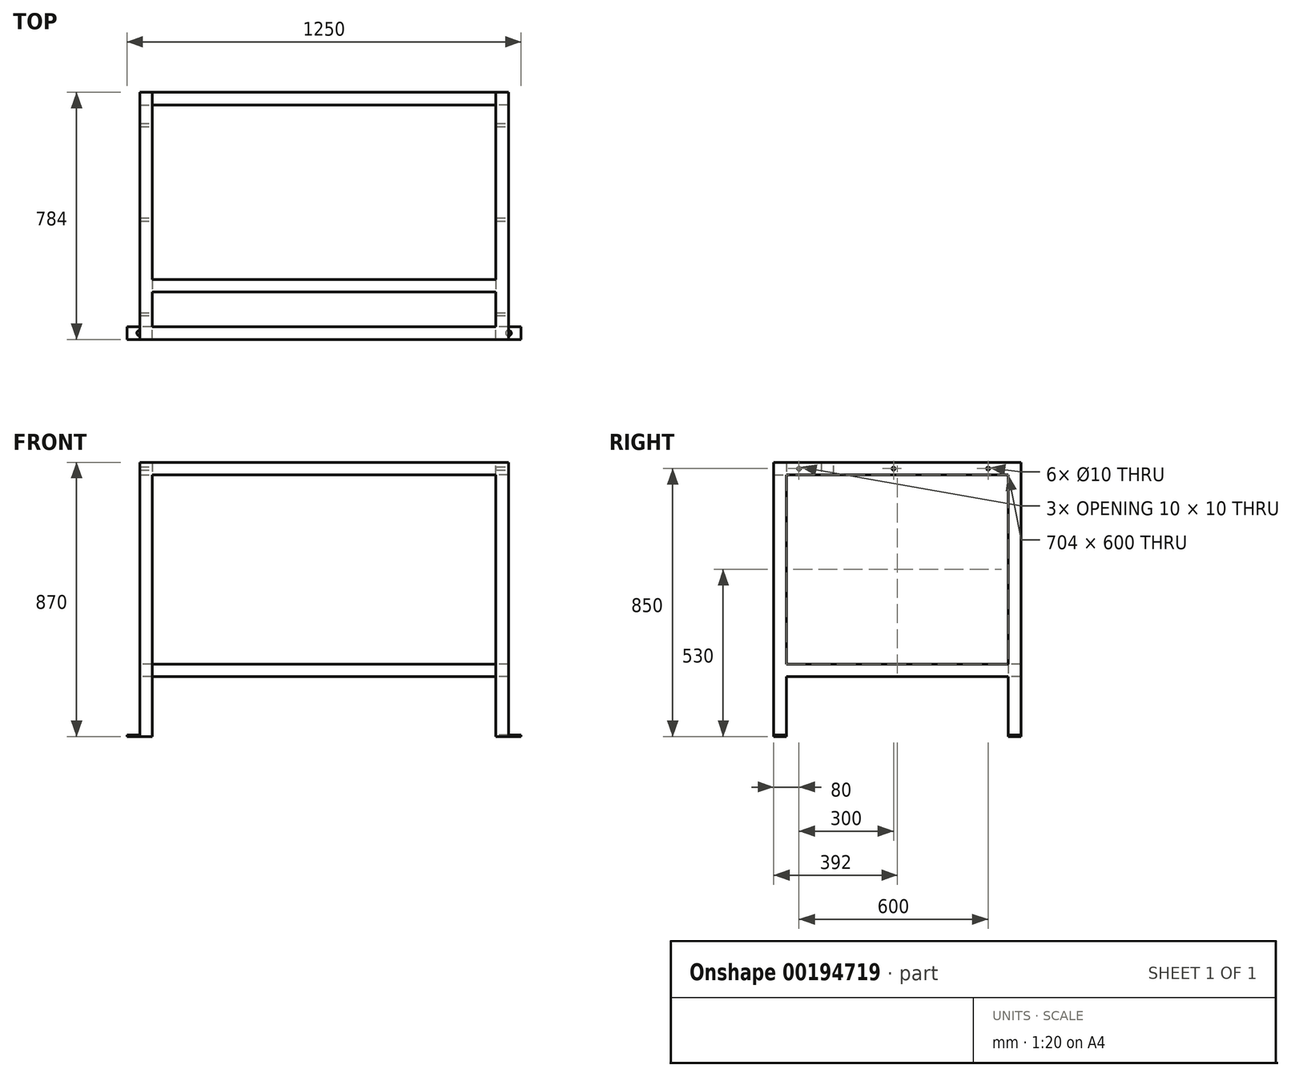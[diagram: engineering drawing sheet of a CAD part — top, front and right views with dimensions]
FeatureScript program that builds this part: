
annotation { "Feature Type Name" : "Feature", "Feature Type Description" : "" }
export const myFeature = defineFeature(function(context is Context, id is Id, definition is map)
    precondition{}
    {
        {
            var Q0;
            Q0=qCreatedBy(makeId("Front.planeOp"),FACE);
            var sketch = newSketch(context, id + "F0", { "sketchPlane" : qUnion([Q0])});
            skLineSegment(sketch, "E0.bottom", {"start": v(-585, -20) * mm, "end": v(585, -20) * mm});
            skLineSegment(sketch, "E0.top", {"start": v(-585, 20) * mm, "end": v(585, 20) * mm});
            skLineSegment(sketch, "E0.left", {"start": v(-585, -20) * mm, "end": v(-585, 20) * mm});
            skLineSegment(sketch, "E0.right", {"start": v(585, -20) * mm, "end": v(585, 20) * mm});
            skPoint(sketch, "E0.middle", {"position": v(0, 0) * mm});
            skLineSegment(sketch, "E1.bottom", {"start": v(-585, -20) * mm, "end": v(-545, -20) * mm});
            skLineSegment(sketch, "E1.top", {"start": v(-585, -850) * mm, "end": v(-545, -850) * mm});
            skLineSegment(sketch, "E1.left", {"start": v(-585, -20) * mm, "end": v(-585, -850) * mm});
            skLineSegment(sketch, "E1.right", {"start": v(-545, -20) * mm, "end": v(-545, -850) * mm});
            skLineSegment(sketch, "E2.bottom", {"start": v(585, -20) * mm, "end": v(545, -20) * mm});
            skLineSegment(sketch, "E2.top", {"start": v(585, -850) * mm, "end": v(545, -850) * mm});
            skLineSegment(sketch, "E2.left", {"start": v(585, -20) * mm, "end": v(585, -850) * mm});
            skLineSegment(sketch, "E2.right", {"start": v(545, -20) * mm, "end": v(545, -850) * mm});
            skLineSegment(sketch, "E3.left", {"start": v(-545, -620) * mm, "end": v(-545, -660) * mm});
            skLineSegment(sketch, "E3.right", {"start": v(545, -620) * mm, "end": v(545, -660) * mm});
            skSolve(sketch);
        }
        {
            var Q0;
            Q0 = qSketchRegion(id + "F0", true);
            extrude(context, id + "F1", {"entities" : qUnion([Q0]), "depth" : 40 * mm});
        }
        {
            var Q0;
            Q0=makeQuery(id+"F1.opExtrude","CAP_FACE",FACE,{"disambiguationData":[OSD([sQuery(id+"F0.wireOp",EDGE,"E0.bottom"),sQuery(id+"F0.wireOp",EDGE,"E0.top"),sQuery(id+"F0.wireOp",EDGE,"E0.left"),sQuery(id+"F0.wireOp",EDGE,"E0.right"),sQuery(id+"F0.wireOp",EDGE,"E1.top"),sQuery(id+"F0.wireOp",EDGE,"E1.left"),sQuery(id+"F0.wireOp",EDGE,"E1.right"),sQuery(id+"F0.wireOp",EDGE,"E2.top"),sQuery(id+"F0.wireOp",EDGE,"E2.left"),sQuery(id+"F0.wireOp",EDGE,"E2.right"),sQuery(id+"F0.wireOp",EDGE,"E3.bottom"),sQuery(id+"F0.wireOp",EDGE,"E3.top")])],"isStart":true});
            var sketch = newSketch(context, id + "F2", { "sketchPlane" : qUnion([Q0])});
            skLineSegment(sketch, "E4.bottom", {"start": v(-585, 20) * mm, "end": v(-545, 20) * mm});
            skLineSegment(sketch, "E4.top", {"start": v(-585, -20) * mm, "end": v(-545, -20) * mm});
            skLineSegment(sketch, "E4.left", {"start": v(-585, 20) * mm, "end": v(-585, -20) * mm});
            skLineSegment(sketch, "E4.right", {"start": v(-545, 20) * mm, "end": v(-545, -20) * mm});
            skLineSegment(sketch, "E5.bottom", {"start": v(585, 20) * mm, "end": v(545, 20) * mm});
            skLineSegment(sketch, "E5.top", {"start": v(585, -20) * mm, "end": v(545, -20) * mm});
            skLineSegment(sketch, "E5.left", {"start": v(585, 20) * mm, "end": v(585, -20) * mm});
            skLineSegment(sketch, "E5.right", {"start": v(545, 20) * mm, "end": v(545, -20) * mm});
            skLineSegment(sketch, "E6.bottom", {"start": v(545, -850) * mm, "end": v(585, -850) * mm});
            skLineSegment(sketch, "E6.top", {"start": v(545, -850) * mm, "end": v(585, -850) * mm});
            skLineSegment(sketch, "E6.left", {"start": v(545, -850) * mm, "end": v(545, -850) * mm});
            skLineSegment(sketch, "E6.right", {"start": v(585, -850) * mm, "end": v(585, -850) * mm});
            skLineSegment(sketch, "E7.bottom", {"start": v(-545, -850) * mm, "end": v(-585, -850) * mm});
            skLineSegment(sketch, "E7.top", {"start": v(-545, -850) * mm, "end": v(-585, -850) * mm});
            skLineSegment(sketch, "E7.left", {"start": v(-545, -850) * mm, "end": v(-545, -850) * mm});
            skLineSegment(sketch, "E7.right", {"start": v(-585, -850) * mm, "end": v(-585, -850) * mm});
            skLineSegment(sketch, "E8.bottom", {"start": v(-585, -620) * mm, "end": v(-545, -620) * mm});
            skLineSegment(sketch, "E8.top", {"start": v(-585, -660) * mm, "end": v(-545, -660) * mm});
            skLineSegment(sketch, "E8.left", {"start": v(-585, -620) * mm, "end": v(-585, -660) * mm});
            skLineSegment(sketch, "E8.right", {"start": v(-545, -620) * mm, "end": v(-545, -660) * mm});
            skLineSegment(sketch, "E9.bottom", {"start": v(545, -620) * mm, "end": v(585, -620) * mm});
            skLineSegment(sketch, "E9.top", {"start": v(545, -660) * mm, "end": v(585, -660) * mm});
            skLineSegment(sketch, "E9.left", {"start": v(545, -620) * mm, "end": v(545, -660) * mm});
            skLineSegment(sketch, "E9.right", {"start": v(585, -620) * mm, "end": v(585, -660) * mm});
            skSolve(sketch);
        }
        {
            var Q0;
            Q0 = qSketchRegion(id + "F2", true);
            extrude(context, id + "F3", {"entities" : qUnion([Q0]), "operationType" : NewBodyOperationType.ADD, "depth" : 704 * mm});
        }
        {
            var Q0;
            Q0=makeQuery(id+"F3.opExtrude","CAP_FACE",FACE,{"disambiguationData":[OSD([sQuery(id+"F2.wireOp",EDGE,"E4.bottom"),sQuery(id+"F2.wireOp",EDGE,"E4.top"),sQuery(id+"F2.wireOp",EDGE,"E4.left"),sQuery(id+"F2.wireOp",EDGE,"E4.right")])],"isStart":false});
            var sketch = newSketch(context, id + "F4", { "sketchPlane" : qUnion([Q0])});
            skLineSegment(sketch, "E10.bottom", {"start": v(-585, 20) * mm, "end": v(-545, 20) * mm});
            skLineSegment(sketch, "E10.top", {"start": v(-585, -850) * mm, "end": v(-545, -850) * mm});
            skLineSegment(sketch, "E10.left", {"start": v(-585, 20) * mm, "end": v(-585, -850) * mm});
            skLineSegment(sketch, "E10.right", {"start": v(-545, 20) * mm, "end": v(-545, -850) * mm});
            skLineSegment(sketch, "E11.bottom", {"start": v(585, 20) * mm, "end": v(545, 20) * mm});
            skLineSegment(sketch, "E11.top", {"start": v(585, -850) * mm, "end": v(545, -850) * mm});
            skLineSegment(sketch, "E11.left", {"start": v(585, 20) * mm, "end": v(585, -850) * mm});
            skLineSegment(sketch, "E11.right", {"start": v(545, 20) * mm, "end": v(545, -850) * mm});
            skLineSegment(sketch, "E12.bottom", {"start": v(585, -620) * mm, "end": v(-545, -620) * mm});
            skLineSegment(sketch, "E12.top", {"start": v(585, -660) * mm, "end": v(-545, -660) * mm});
            skLineSegment(sketch, "E12.left", {"start": v(585, -620) * mm, "end": v(585, -660) * mm});
            skLineSegment(sketch, "E12.right", {"start": v(-545, -620) * mm, "end": v(-545, -660) * mm});
            skSolve(sketch);
        }
        {
            var Q0;
            Q0 = qSketchRegion(id + "F4", true);
            extrude(context, id + "F5", {"entities" : qUnion([Q0]), "operationType" : NewBodyOperationType.ADD, "depth" : 40 * mm});
        }
        {
            var Q0;
            Q0=makeQuery(id+"F3.boolean.opBoolean","MERGE",FACE,{"derivedFrom":[makeQuery(id+"F1.opExtrude","SWEPT_FACE",FACE,{"disambiguationData":[OSD([sQuery(id+"F0.wireOp",EDGE,"E2.right"),sQuery(id+"F0.wireOp",EDGE,"E3.right")])]}),makeQuery(id+"F3.opExtrude","SWEPT_FACE",FACE,{"disambiguationData":[OSD([sQuery(id+"F2.wireOp",EDGE,"E8.right")])]})]});
            var sketch = newSketch(context, id + "F6", { "sketchPlane" : qUnion([Q0])});
            skLineSegment(sketch, "E13.bottom", {"start": v(40, -850) * mm, "end": v(0, -850) * mm});
            skLineSegment(sketch, "E13.top", {"start": v(40, -845) * mm, "end": v(0, -845) * mm});
            skLineSegment(sketch, "E13.left", {"start": v(40, -850) * mm, "end": v(40, -845) * mm});
            skLineSegment(sketch, "E13.right", {"start": v(0, -850) * mm, "end": v(0, -845) * mm});
            skLineSegment(sketch, "E14.bottom", {"start": v(-704, -850) * mm, "end": v(-744, -850) * mm});
            skLineSegment(sketch, "E14.top", {"start": v(-704, -845) * mm, "end": v(-744, -845) * mm});
            skLineSegment(sketch, "E14.left", {"start": v(-704, -850) * mm, "end": v(-704, -845) * mm});
            skLineSegment(sketch, "E14.right", {"start": v(-744, -850) * mm, "end": v(-744, -845) * mm});
            skSolve(sketch);
        }
        {
            var Q0;
            Q0 = qSketchRegion(id + "F6", true);
            extrude(context, id + "F7", {"entities" : qUnion([Q0]), "oppositeDirection" : true, "depth" : 80 * mm});
        }
        {
            var Q0;
            Q0=makeQuery(id+"F7.opExtrude","SWEPT_FACE",FACE,{"disambiguationData":[OSD([sQuery(id+"F6.wireOp",EDGE,"E13.top")])]});
            var sketch = newSketch(context, id + "F8", { "sketchPlane" : qUnion([Q0])});
            skCircle(sketch, "E15", {"center": v(585, -20) * mm, "radius": 9 * mm});
            skPoint(sketch, "E15.centerSnap0", {"position": v(585, -40) * mm});
            skCircle(sketch, "E16", {"center": v(605, 704) * mm, "radius": 9 * mm});
            skSolve(sketch);
        }
        {
            var Q0;
            Q0=makeQuery(id+"F8.imprint","IMPRINT",FACE,{"disambiguationData":[TD([[makeQuery(id+"F8.imprint","IMPRINT",EDGE,{"derivedFrom":sQuery(id+"F8.wireOp",EDGE,"E15")}),1.0]])]});
            var Q1;
            Q1=makeQuery(id+"F7.opExtrude","SWEPT_FACE",FACE,{"disambiguationData":[OSD([sQuery(id+"F6.wireOp",EDGE,"E14.top")])]});
            extrude(context, id + "F9", {"entities" : qUnion([Q0, Q1]), "operationType" : NewBodyOperationType.REMOVE, "oppositeDirection" : true, "depth" : 30 * mm});
        }
        {
            var Q0;
            Q0=makeQuery(id+"F7.opExtrude","SWEPT_BODY",BODY,{"disambiguationData":[OSD([sQuery(id+"F6.wireOp",EDGE,"E13.bottom"),sQuery(id+"F6.wireOp",EDGE,"E13.top"),sQuery(id+"F6.wireOp",EDGE,"E13.left"),sQuery(id+"F6.wireOp",EDGE,"E13.right")])]});
            var Q1;
            Q1=makeQuery(id+"F7.opExtrude","SWEPT_BODY",BODY,{"disambiguationData":[OSD([sQuery(id+"F6.wireOp",EDGE,"E14.bottom"),sQuery(id+"F6.wireOp",EDGE,"E14.top"),sQuery(id+"F6.wireOp",EDGE,"E14.left"),sQuery(id+"F6.wireOp",EDGE,"E14.right")])]});
            var Q2;
            Q2=qCreatedBy(makeId("Right.planeOp"),FACE);
            mirror(context, id + "F10", {"operationType" : NewBodyOperationType.ADD, "entities" : qUnion([Q0, Q1]), "mirrorPlane" : qUnion([Q2])});
        }
        {
            var Q0;
            {var subQ0=sQuery(id+"F4.wireOp",EDGE,"E11.right");Q0=makeQuery(id+"F5.boolean.opBoolean","MERGE",FACE,{"derivedFrom":[makeQuery(id+"F3.opExtrude","SWEPT_FACE",FACE,{"disambiguationData":[OSD([sQuery(id+"F2.wireOp",EDGE,"E5.right")])]}),makeQuery(id+"F5.opExtrude","SWEPT_FACE",FACE,{"disambiguationData":[OSD([subQ0]),TDD([makeQuery(id+"F4.imprint","IMPRINT",EDGE,{"disambiguationData":[TD([[makeQuery(id+"F4.imprint","INTERSECT",VERTEX,{"derivedFrom":[sQuery(id+"F4.wireOp",EDGE,"E11.bottom"),subQ0]}),-1.0]])],"derivedFrom":subQ0})])]})]});}
            var sketch = newSketch(context, id + "F11", { "sketchPlane" : qUnion([Q0])});
            skLineSegment(sketch, "E17.bottom", {"start": v(110, 20) * mm, "end": v(150, 20) * mm});
            skLineSegment(sketch, "E17.top", {"start": v(110, -20) * mm, "end": v(150, -20) * mm});
            skLineSegment(sketch, "E17.left", {"start": v(110, 20) * mm, "end": v(110, -20) * mm});
            skLineSegment(sketch, "E17.right", {"start": v(150, 20) * mm, "end": v(150, -20) * mm});
            skSolve(sketch);
        }
        {
            var Q0;
            Q0 = qSketchRegion(id + "F11", true);
            extrude(context, id + "F12", {"entities" : qUnion([Q0]), "operationType" : NewBodyOperationType.ADD, "endBound" : BoundingType.UP_TO_NEXT, "depth" : 25 * mm});
        }
        {
            var Q0;
            Q0=makeQuery(id+"F5.boolean.opBoolean","MERGE",FACE,{"derivedFrom":[makeQuery(id+"F3.boolean.opBoolean","MERGE",FACE,{"derivedFrom":[makeQuery(id+"F1.opExtrude","SWEPT_FACE",FACE,{"disambiguationData":[OSD([sQuery(id+"F0.wireOp",EDGE,"E0.right"),sQuery(id+"F0.wireOp",EDGE,"E2.left")])]}),makeQuery(id+"F3.opExtrude","SWEPT_FACE",FACE,{"disambiguationData":[OSD([sQuery(id+"F2.wireOp",EDGE,"E4.left")])]}),makeQuery(id+"F3.opExtrude","SWEPT_FACE",FACE,{"disambiguationData":[OSD([sQuery(id+"F2.wireOp",EDGE,"E8.left")])]})]}),makeQuery(id+"F5.opExtrude","SWEPT_FACE",FACE,{"disambiguationData":[OSD([sQuery(id+"F4.wireOp",EDGE,"E10.left")])]})]});
            var sketch = newSketch(context, id + "F13", { "sketchPlane" : qUnion([Q0])});
            skCircle(sketch, "E18", {"center": v(340, 0) * mm, "radius": 5 * mm});
            skCircle(sketch, "E19", {"center": v(640, 0) * mm, "radius": 5 * mm});
            skCircle(sketch, "E20", {"center": v(40, 0) * mm, "radius": 5 * mm});
            skSolve(sketch);
        }
        {
            var Q0;
            Q0 = qSketchRegion(id + "F13", true);
            var Q1;
            Q1=makeQuery(id+"F5.boolean.opBoolean","MERGE",FACE,{"derivedFrom":[makeQuery(id+"F3.boolean.opBoolean","MERGE",FACE,{"derivedFrom":[makeQuery(id+"F1.opExtrude","SWEPT_FACE",FACE,{"disambiguationData":[OSD([sQuery(id+"F0.wireOp",EDGE,"E0.left"),sQuery(id+"F0.wireOp",EDGE,"E1.left")])]}),makeQuery(id+"F3.opExtrude","SWEPT_FACE",FACE,{"disambiguationData":[OSD([sQuery(id+"F2.wireOp",EDGE,"E5.left")])]}),makeQuery(id+"F3.opExtrude","SWEPT_FACE",FACE,{"disambiguationData":[OSD([sQuery(id+"F2.wireOp",EDGE,"E9.right")])]})]}),makeQuery(id+"F5.opExtrude","SWEPT_FACE",FACE,{"disambiguationData":[OSD([sQuery(id+"F4.wireOp",EDGE,"E11.left"),sQuery(id+"F4.wireOp",EDGE,"E12.left")])]})]});
            extrude(context, id + "F14", {"entities" : qUnion([Q0]), "operationType" : NewBodyOperationType.REMOVE, "endBound" : BoundingType.UP_TO_SURFACE, "oppositeDirection" : true, "depth" : 25 * mm, "endBoundEntityFace" : qUnion([Q1]), "offsetDistance" : 25 * mm});
        }
    });
